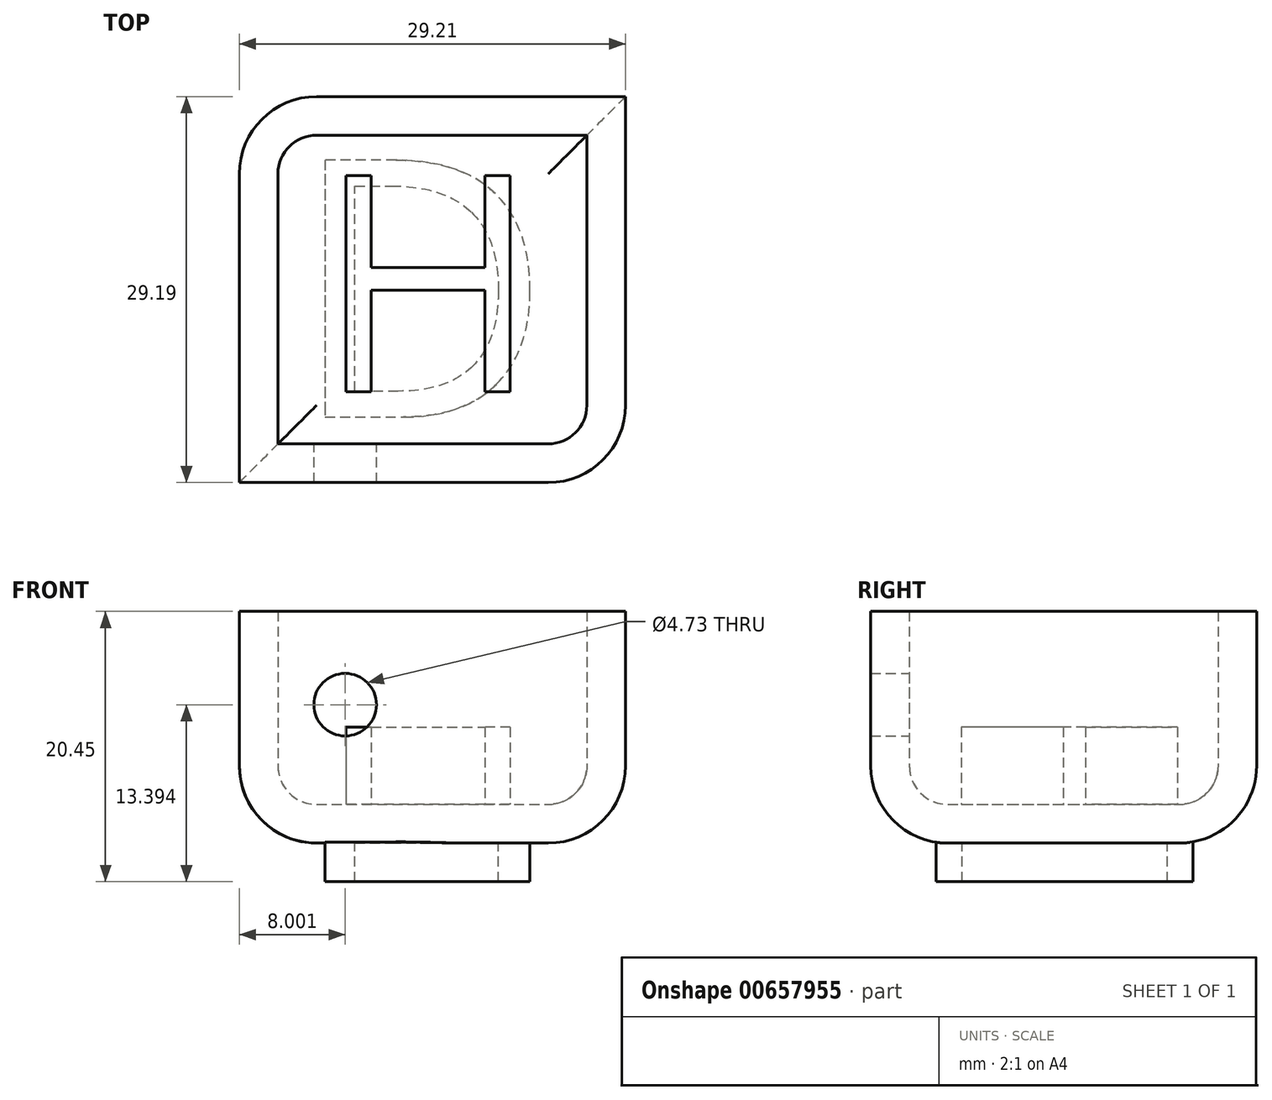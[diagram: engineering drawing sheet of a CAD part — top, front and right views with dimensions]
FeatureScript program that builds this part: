
annotation { "Feature Type Name" : "Feature", "Feature Type Description" : "" }
export const myFeature = defineFeature(function(context is Context, id is Id, definition is map)
    precondition{}
    {
        {
            var Q0;
            Q0=qCreatedBy(makeId("Top.planeOp"),FACE);
            var sketch = newSketch(context, id + "F0", { "sketchPlane" : qUnion([Q0])});
            skLineSegment(sketch, "E0.bottom", {"start": v(-17.43, -9.78) * mm, "end": v(-4.73, -9.78) * mm});
            skLineSegment(sketch, "E0.top", {"start": v(-17.43, 2.91) * mm, "end": v(-4.73, 2.91) * mm});
            skLineSegment(sketch, "E0.left", {"start": v(-17.43, -9.78) * mm, "end": v(-17.43, 2.91) * mm});
            skLineSegment(sketch, "E0.right", {"start": v(-4.73, -9.78) * mm, "end": v(-4.73, 2.91) * mm});
            skSolve(sketch);
        }
        {
            var Q0;
            Q0=makeQuery(id+"F0.imprint","IMPRINT",FACE,{"disambiguationData":[TD([[makeQuery(id+"F0.imprint","IMPRINT",EDGE,{"derivedFrom":sQuery(id+"F0.wireOp",EDGE,"E0.bottom")}),1.0]])]});
            extrude(context, id + "F1", {"entities" : qUnion([Q0]), "depth" : 7.62 * mm, "offsetDistance" : 25.4 * mm});
        }
        {
            var Q0;
            Q0=makeQuery(id+"F1.opExtrude","CAP_FACE",FACE,{"disambiguationData":[OSD([sQuery(id+"F0.wireOp",EDGE,"E0.bottom"),sQuery(id+"F0.wireOp",EDGE,"E0.top"),sQuery(id+"F0.wireOp",EDGE,"E0.left"),sQuery(id+"F0.wireOp",EDGE,"E0.right")])],"isStart":true});
            var sketch = newSketch(context, id + "F2", { "sketchPlane" : qUnion([Q0])});
            skText(sketch, "E1", { "text": "D", "fontName": "OpenSans-Regular.ttf"});
            const initialGuessF2  = {"E1": [-0.01578, -0.00082, 1, 0, 0.00852]};
            skSetInitialGuess(sketch, initialGuessF2);
            skSolve(sketch);
        }
        {
            var Q0;
            Q0=makeQuery(id+"F1.opExtrude","CAP_FACE",FACE,{"disambiguationData":[OSD([sQuery(id+"F0.wireOp",EDGE,"E0.bottom"),sQuery(id+"F0.wireOp",EDGE,"E0.top"),sQuery(id+"F0.wireOp",EDGE,"E0.left"),sQuery(id+"F0.wireOp",EDGE,"E0.right")])],"isStart":false});
            var sketch = newSketch(context, id + "F3", { "sketchPlane" : qUnion([Q0])});
            skText(sketch, "E2", { "text": "E", "fontName": "OpenSans-Regular.ttf"});
            const initialGuessF3  = {"E2": [-0.01606, -0.00814, 1, 0, 0.00934]};
            skSetInitialGuess(sketch, initialGuessF3);
            skSolve(sketch);
        }
        {
            var Q0;
            Q0=makeQuery(id+"F2.imprint","IMPRINT",FACE,{"disambiguationData":[TD([[makeQuery(id+"F2.imprint","IMPRINT",EDGE,{"derivedFrom":sQuery(id+"F2.wireOp",EDGE,"E1.sketch_text.stroke-0")}),-1.0]])]});
            extrude(context, id + "F4", {"entities" : qUnion([Q0]), "operationType" : NewBodyOperationType.ADD, "depth" : 1.27 * mm, "offsetDistance" : 25.4 * mm});
        }
        {
            var Q0;
            Q0=makeQuery(id+"F3.imprint","IMPRINT",FACE,{"disambiguationData":[TD([[makeQuery(id+"F3.imprint","IMPRINT",EDGE,{"derivedFrom":sQuery(id+"F3.wireOp",EDGE,"E2.sketch_text.stroke-0")}),-1.0]])]});
            extrude(context, id + "F5", {"entities" : qUnion([Q0]), "operationType" : NewBodyOperationType.REMOVE, "depth" : 2.54 * mm, "offsetDistance" : 25.4 * mm});
        }
        {
            var Q0;
            Q0=makeQuery(id+"F1.opExtrude","CAP_FACE",FACE,{"disambiguationData":[OSD([sQuery(id+"F0.wireOp",EDGE,"E0.bottom"),sQuery(id+"F0.wireOp",EDGE,"E0.top"),sQuery(id+"F0.wireOp",EDGE,"E0.left"),sQuery(id+"F0.wireOp",EDGE,"E0.right")])],"isStart":false});
            var sketch = newSketch(context, id + "F6", { "sketchPlane" : qUnion([Q0])});
            skCircle(sketch, "E3", {"center": v(-6.8, 1.07) * mm, "radius": 1.45 * mm});
            skSolve(sketch);
        }
        {
            var Q0;
            Q0=makeQuery(id+"F6.imprint","IMPRINT",FACE,{"disambiguationData":[TD([[makeQuery(id+"F6.imprint","IMPRINT",EDGE,{"derivedFrom":sQuery(id+"F6.wireOp",EDGE,"E3")}),1.0]])]});
            extrude(context, id + "F7", {"entities" : qUnion([Q0]), "operationType" : NewBodyOperationType.ADD, "oppositeDirection" : true, "depth" : 5.08 * mm, "offsetDistance" : 25.4 * mm});
        }
        {
            var Q0;
            Q0=makeQuery(id+"F1.opExtrude","CAP_EDGE",EDGE,{"disambiguationData":[OSD([sQuery(id+"F0.wireOp",EDGE,"E0.right")])],"isStart":true});
            var Q1;
            Q1=makeQuery(id+"F1.opExtrude","CAP_EDGE",EDGE,{"disambiguationData":[OSD([sQuery(id+"F0.wireOp",EDGE,"E0.top")])],"isStart":true});
            fillet(context, id + "F8", {"entities" : qUnion([Q0, Q1]), "radius" : 2.54 * mm, "tangentPropagation" : true, "allowEdgeOverflow" : false});
        }
        {
            var Q0;
            Q0=makeQuery(id+"F1.opExtrude","CAP_EDGE",EDGE,{"disambiguationData":[OSD([sQuery(id+"F0.wireOp",EDGE,"E0.bottom")])],"isStart":true});
            var Q1;
            Q1=makeQuery(id+"F1.opExtrude","CAP_EDGE",EDGE,{"disambiguationData":[OSD([sQuery(id+"F0.wireOp",EDGE,"E0.left")])],"isStart":true});
            fillet(context, id + "F9", {"entities" : qUnion([Q0, Q1]), "radius" : 2.54 * mm, "tangentPropagation" : true, "allowEdgeOverflow" : false});
        }
        {
            var Q0;
            Q0=makeQuery(id+"F1.opExtrude","CAP_FACE",FACE,{"disambiguationData":[OSD([sQuery(id+"F0.wireOp",EDGE,"E0.bottom"),sQuery(id+"F0.wireOp",EDGE,"E0.top"),sQuery(id+"F0.wireOp",EDGE,"E0.left"),sQuery(id+"F0.wireOp",EDGE,"E0.right")])],"isStart":false});
            shell(context, id + "F10", {"entities" : qUnion([Q0]), "thickness" : 1.27 * mm});
        }
        {
            var Q0;
            Q0=makeQuery(id+"F10.opShell","OFFSET_FACE",FACE,{"disambiguationData":[OSD([sQuery(id+"F0.wireOp",EDGE,"E0.bottom"),sQuery(id+"F0.wireOp",EDGE,"E0.top"),sQuery(id+"F0.wireOp",EDGE,"E0.left"),sQuery(id+"F0.wireOp",EDGE,"E0.right"),sQuery(id+"F2.wireOp",EDGE,"E1.sketch_text.stroke-3")])]});
            var sketch = newSketch(context, id + "F11", { "sketchPlane" : qUnion([Q0])});
            skText(sketch, "E4", { "text": "H", "fontName": "OpenSans-Regular.ttf"});
            const initialGuessF11  = {"E4": [-0.0149, -0.0068, 1, 0, 0.00717]};
            skSetInitialGuess(sketch, initialGuessF11);
            skSolve(sketch);
        }
        {
            var Q0;
            Q0=makeQuery(id+"F11.imprint","IMPRINT",FACE,{"disambiguationData":[TD([[makeQuery(id+"F11.imprint","IMPRINT",EDGE,{"derivedFrom":sQuery(id+"F11.wireOp",EDGE,"E4.sketch_text.stroke-0")}),-1.0]])]});
            extrude(context, id + "F12", {"entities" : qUnion([Q0]), "operationType" : NewBodyOperationType.ADD, "depth" : 2.54 * mm, "offsetDistance" : 25.4 * mm});
        }
        {
            var Q0;
            {var subQ0=sQuery(id+"F0.wireOp",EDGE,"E0.bottom");Q0=makeQuery(id+"F10.opShell","OFFSET_FACE",FACE,{"disambiguationData":[OSD([subQ0]),TDD([makeQuery(id+"F1.opExtrude","SWEPT_FACE",FACE,{"disambiguationData":[OSD([subQ0])]})])]});}
            var sketch = newSketch(context, id + "F13", { "sketchPlane" : qUnion([Q0])});
            skCircle(sketch, "E5", {"center": v(13.95, 4.55) * mm, "radius": 1.03 * mm});
            skSolve(sketch);
        }
        {
            var Q0;
            Q0=makeQuery(id+"F13.imprint","IMPRINT",FACE,{"disambiguationData":[TD([[makeQuery(id+"F13.imprint","IMPRINT",EDGE,{"derivedFrom":sQuery(id+"F13.wireOp",EDGE,"E5")}),1.0]])]});
            extrude(context, id + "F14", {"entities" : qUnion([Q0]), "operationType" : NewBodyOperationType.REMOVE, "oppositeDirection" : true, "depth" : 25.4 * mm, "offsetDistance" : 25.4 * mm});
        }
        {
            var Q0;
            Q0=makeQuery(id+"F1.opExtrude","SWEPT_BODY",BODY,{"disambiguationData":[OSD([sQuery(id+"F0.wireOp",EDGE,"E0.bottom"),sQuery(id+"F0.wireOp",EDGE,"E0.top"),sQuery(id+"F0.wireOp",EDGE,"E0.left"),sQuery(id+"F0.wireOp",EDGE,"E0.right")])]});
            var Q1;
            {var subQ0=sQuery(id+"F0.wireOp",EDGE,"E0.bottom");var subQ1=sQuery(id+"F0.wireOp",EDGE,"E0.right");Q1=makeQuery(id+"F9.opFillet","BLEND_VERTEX",VERTEX,{"blendedFrom":[makeQuery(id+"F1.opExtrude","SWEPT_EDGE",EDGE,{"disambiguationData":[OSD([subQ0,subQ1])]}),makeQuery(id+"F1.opExtrude","CAP_FACE",FACE,{"disambiguationData":[OSD([subQ0,sQuery(id+"F0.wireOp",EDGE,"E0.top"),sQuery(id+"F0.wireOp",EDGE,"E0.left"),subQ1])],"isStart":false}),makeQuery(id+"F1.opExtrude","SWEPT_FACE",FACE,{"disambiguationData":[OSD([subQ0])]})],"blendedInto":[makeQuery(id+"F1.opExtrude","CAP_FACE",FACE,{"disambiguationData":[OSD([subQ0,sQuery(id+"F0.wireOp",EDGE,"E0.top"),sQuery(id+"F0.wireOp",EDGE,"E0.left"),subQ1])],"isStart":false}),makeQuery(id+"F1.opExtrude","SWEPT_FACE",FACE,{"disambiguationData":[OSD([subQ0])]})]});}
            transform(context, id + "F15", {"entities" : qUnion([Q0]), "transformType" : TransformType.SCALE_UNIFORMLY, "scale" : 2.3, "scalePoint" : qUnion([Q1]), "makeCopy" : false});
        }
    });
